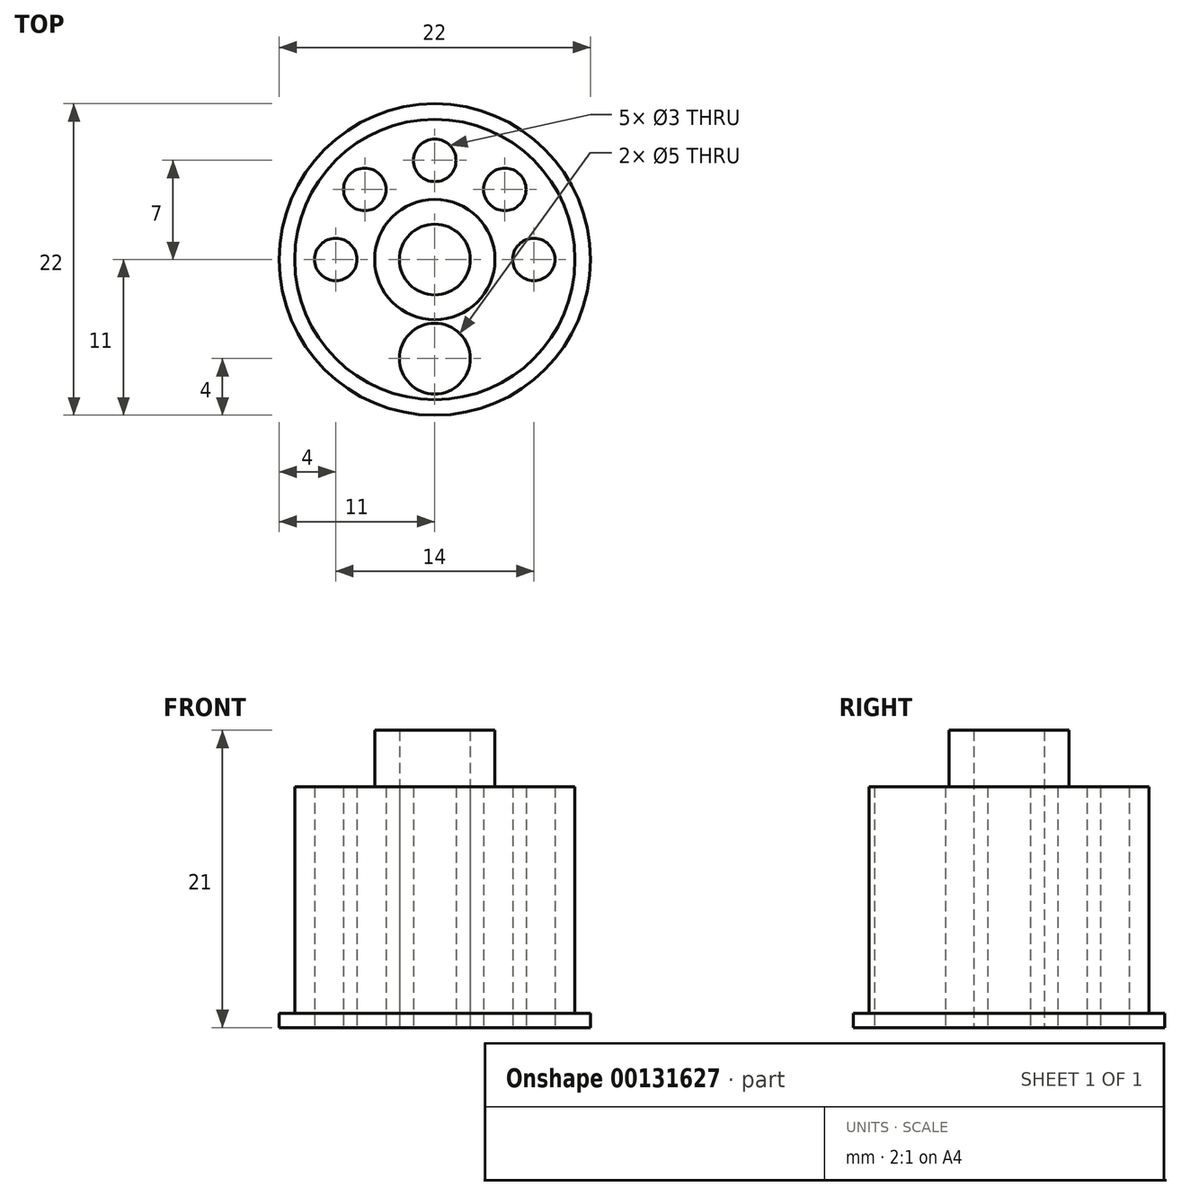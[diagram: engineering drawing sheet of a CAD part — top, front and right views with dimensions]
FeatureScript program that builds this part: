
annotation { "Feature Type Name" : "Feature", "Feature Type Description" : "" }
export const myFeature = defineFeature(function(context is Context, id is Id, definition is map)
    precondition{}
    {
        {
            var Q0;
            Q0=qCreatedBy(makeId("Top.planeOp"),FACE);
            var sketch = newSketch(context, id + "F0", { "sketchPlane" : qUnion([Q0])});
            skCircle(sketch, "E0", {"center": v(0, 0) * mm, "radius": 11 * mm});
            skCircle(sketch, "E1", {"center": v(0, 0) * mm, "radius": 9.9 * mm});
            skCircle(sketch, "E2", {"center": v(0, 0) * mm, "radius": 4.25 * mm});
            skCircle(sketch, "E3", {"center": v(0, 0) * mm, "radius": 2.5 * mm});
            skCircle(sketch, "E4", {"center": v(0, -7) * mm, "radius": 2.5 * mm});
            skCircle(sketch, "E5", {"center": v(0, 0) * mm, "radius": 7 * mm, "construction": true});
            skCircle(sketch, "E6", {"center": v(-7, 0) * mm, "radius": 1.5 * mm});
            skCircle(sketch, "E7", {"center": v(7, 0) * mm, "radius": 1.5 * mm});
            skCircle(sketch, "E8", {"center": v(0, 7) * mm, "radius": 1.5 * mm});
            skCircle(sketch, "E9", {"center": v(4.95, 4.95) * mm, "radius": 1.5 * mm});
            skCircle(sketch, "E10.MirrorC", {"center": v(-4.95, 4.95) * mm, "radius": 1.5 * mm});
            skSolve(sketch);
        }
        {
            var Q0;
            Q0=makeQuery(id+"F0.imprint","IMPRINT",FACE,{"disambiguationData":[TD([[makeQuery(id+"F0.imprint","IMPRINT",EDGE,{"derivedFrom":sQuery(id+"F0.wireOp",EDGE,"E2")}),1.0]])]});
            extrude(context, id + "F1", {"entities" : qUnion([Q0]), "depth" : 21 * mm});
        }
        {
            var Q0;
            Q0=makeQuery(id+"F0.imprint","IMPRINT",FACE,{"disambiguationData":[TD([[makeQuery(id+"F0.imprint","IMPRINT",EDGE,{"derivedFrom":sQuery(id+"F0.wireOp",EDGE,"E1")}),1.0]])]});
            extrude(context, id + "F2", {"entities" : qUnion([Q0]), "operationType" : NewBodyOperationType.ADD, "depth" : 17 * mm});
        }
        {
            var Q0;
            Q0=makeQuery(id+"F0.imprint","IMPRINT",FACE,{"disambiguationData":[TD([[makeQuery(id+"F0.imprint","IMPRINT",EDGE,{"derivedFrom":sQuery(id+"F0.wireOp",EDGE,"E0")}),1.0]])]});
            extrude(context, id + "F3", {"entities" : qUnion([Q0]), "operationType" : NewBodyOperationType.ADD, "depth" : 1 * mm});
        }
    });
